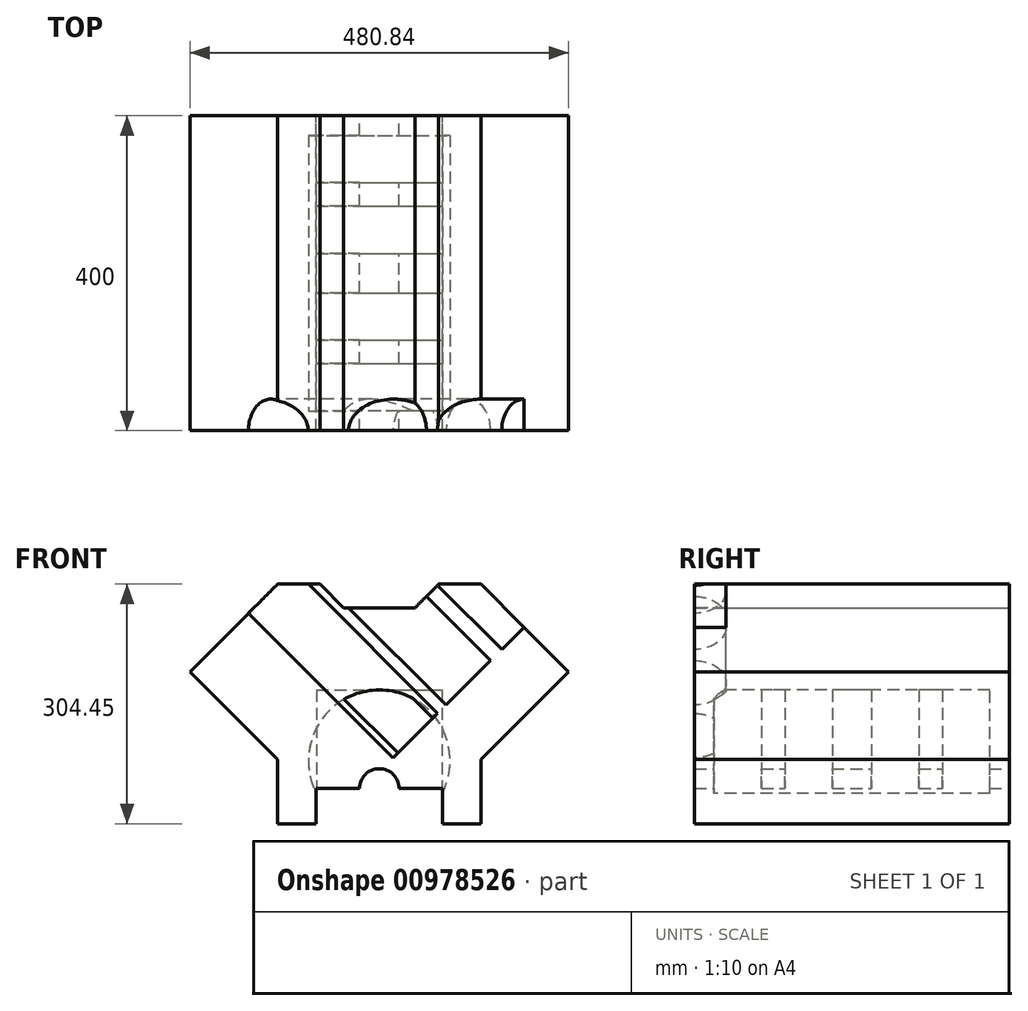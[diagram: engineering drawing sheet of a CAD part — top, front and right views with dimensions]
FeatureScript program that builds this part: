
annotation { "Feature Type Name" : "Feature", "Feature Type Description" : "" }
export const myFeature = defineFeature(function(context is Context, id is Id, definition is map)
    precondition{}
    {
        {
            var Q0;
            Q0=qCreatedBy(makeId("Front.planeOp"),FACE);
            var sketch = newSketch(context, id + "F0", { "sketchPlane" : qUnion([Q0])});
            skCircle(sketch, "E0", {"center": v(0, 0) * mm, "radius": 25 * mm});
            skLineSegment(sketch, "E1", {"start": v(0, 0) * mm, "end": v(-25, 0) * mm});
            skLineSegment(sketch, "E2", {"start": v(0, 0) * mm, "end": v(0, 157.92) * mm, "construction": true});
            skLineSegment(sketch, "E3", {"start": v(0, 0) * mm, "end": v(-17.68, 17.68) * mm, "construction": true});
            skLineSegment(sketch, "E4", {"start": v(0, 0) * mm, "end": v(28.28, 28.28) * mm, "construction": true});
            skLineSegment(sketch, "E5.0", {"start": v(-79.55, -80) * mm, "end": v(-129.1, -80) * mm});
            skLineSegment(sketch, "E6", {"start": v(-240.42, 113.14) * mm, "end": v(-148.5, 205.06) * mm, "construction": true});
            skLineSegment(sketch, "E7", {"start": v(0, 157.92) * mm, "end": v(0, 224.45) * mm, "construction": true});
            skLineSegment(sketch, "E8", {"start": v(-148.5, 205.06) * mm, "end": v(-129.1, 224.45) * mm, "construction": true});
            skLineSegment(sketch, "E9", {"start": v(-129.1, 224.45) * mm, "end": v(0, 224.45) * mm, "construction": true});
            skLineSegment(sketch, "E10", {"start": v(-129.1, 1.82) * mm, "end": v(-129.1, -40) * mm, "construction": true});
            skLineSegment(sketch, "E11", {"start": v(-129.1, -40) * mm, "end": v(-129.1, -80) * mm, "construction": true});
            skLineSegment(sketch, "E12.trimOffspring", {"start": v(-129.1, 1.82) * mm, "end": v(-240.42, 113.14) * mm});
            skLineSegment(sketch, "E13", {"start": v(0, 224.45) * mm, "end": v(-129.1, 224.45) * mm});
            skLineSegment(sketch, "E14", {"start": v(-240.42, 113.14) * mm, "end": v(-129.1, 224.45) * mm});
            skLineSegment(sketch, "E15", {"start": v(-129.1, 1.82) * mm, "end": v(-129.1, -80) * mm});
            skLineSegment(sketch, "E16.MirrorCS", {"start": v(129.1, 224.45) * mm, "end": v(0, 224.45) * mm, "construction": true});
            skLineSegment(sketch, "E17.MirrorCS", {"start": v(148.5, 205.06) * mm, "end": v(129.1, 224.45) * mm, "construction": true});
            skLineSegment(sketch, "E18.MirrorCS", {"start": v(240.42, 113.14) * mm, "end": v(148.5, 205.06) * mm, "construction": true});
            skLineSegment(sketch, "E19.MirrorCS", {"start": v(129.1, 1.82) * mm, "end": v(240.42, 113.14) * mm});
            skLineSegment(sketch, "E20.MirrorCS", {"start": v(129.1, 1.82) * mm, "end": v(129.1, -40) * mm, "construction": true});
            skLineSegment(sketch, "E21.MirrorCS", {"start": v(129.1, -40) * mm, "end": v(129.1, -80) * mm, "construction": true});
            skLineSegment(sketch, "E22.MirrorCS", {"start": v(79.55, -80) * mm, "end": v(129.1, -80) * mm});
            skPoint(sketch, "E23.cornerSnap0", {"position": v(79.55, -80) * mm});
            skPoint(sketch, "E24.MirrorCS.end.orphan", {"position": v(30, -80) * mm});
            skLineSegment(sketch, "E25", {"start": v(-79.55, -80) * mm, "end": v(-79.55, -39.1) * mm});
            skPoint(sketch, "E25.endSnap0", {"position": v(-129.1, -39.1) * mm});
            skLineSegment(sketch, "E26", {"start": v(79.55, -40) * mm, "end": v(79.55, -80) * mm});
            skArc(sketch, "E27", {"start": v(79.55, -42.1) * mm, "mid": v(0, 90) * mm, "end": v(-79.55, -42.1) * mm});
            skLineSegment(sketch, "E28", {"start": v(0, 0) * mm, "end": v(256.96, 256.96) * mm, "construction": true});
            skLineSegment(sketch, "E29", {"start": v(0, 0) * mm, "end": v(-256.18, 256.18) * mm, "construction": true});
            skLineSegment(sketch, "E30", {"start": v(0, 224.45) * mm, "end": v(129.1, 224.45) * mm});
            skLineSegment(sketch, "E31", {"start": v(240.42, 113.14) * mm, "end": v(129.1, 224.45) * mm});
            skLineSegment(sketch, "E32", {"start": v(129.1, 1.82) * mm, "end": v(129.1, -80) * mm});
            skSolve(sketch);
        }
        {
            var Q0;
            {var subQ4=sQuery(id+"F0.wireOp",EDGE,"E5.0");Q0=makeQuery(id+"F0.imprint","IMPRINT",FACE,{"disambiguationData":[TD([[makeQuery(id+"F0.imprint","IMPRINT",EDGE,{"derivedFrom":subQ4}),-1.0]])]});}
            extrude(context, id + "F1", {"entities" : qUnion([Q0]), "oppositeDirection" : true, "depth" : 400 * mm, "offsetDistance" : 25 * mm});
        }
        {
            var Q0;
            Q0=makeQuery(id+"F1.opExtrude","CAP_FACE",FACE,{"disambiguationData":[OSD([sQuery(id+"F0.wireOp",EDGE,"E5.0"),sQuery(id+"F0.wireOp",EDGE,"E12.trimOffspring"),sQuery(id+"F0.wireOp",EDGE,"E13"),sQuery(id+"F0.wireOp",EDGE,"E14"),sQuery(id+"F0.wireOp",EDGE,"E15"),sQuery(id+"F0.wireOp",EDGE,"E19.MirrorCS"),sQuery(id+"F0.wireOp",EDGE,"E22.MirrorCS"),sQuery(id+"F0.wireOp",EDGE,"E25"),sQuery(id+"F0.wireOp",EDGE,"E26"),sQuery(id+"F0.wireOp",EDGE,"E27"),sQuery(id+"F0.wireOp",EDGE,"E30"),sQuery(id+"F0.wireOp",EDGE,"E31"),sQuery(id+"F0.wireOp",EDGE,"E32")])],"isStart":true});
            var sketch = newSketch(context, id + "F2", { "sketchPlane" : qUnion([Q0])});
            skLineSegment(sketch, "E33.bottom", {"start": v(-100.58, 95.3) * mm, "end": v(104.32, 95.3) * mm});
            skLineSegment(sketch, "E33.top", {"start": v(-100.58, -80) * mm, "end": v(104.32, -80) * mm});
            skLineSegment(sketch, "E33.left", {"start": v(-100.58, 95.3) * mm, "end": v(-100.58, -80) * mm});
            skLineSegment(sketch, "E33.right", {"start": v(104.32, 95.3) * mm, "end": v(104.32, -80) * mm});
            skSolve(sketch);
        }
        {
            var Q0;
            Q0 = qSketchRegion(id + "F2", true);
            extrude(context, id + "F3", {"entities" : qUnion([Q0]), "operationType" : NewBodyOperationType.ADD, "oppositeDirection" : true, "depth" : 25 * mm, "offsetDistance" : 25 * mm});
        }
        {
            var Q0;
            Q0=makeQuery(id+"F1.opExtrude","CAP_FACE",FACE,{"disambiguationData":[OSD([sQuery(id+"F0.wireOp",EDGE,"E5.0"),sQuery(id+"F0.wireOp",EDGE,"E12.trimOffspring"),sQuery(id+"F0.wireOp",EDGE,"E13"),sQuery(id+"F0.wireOp",EDGE,"E14"),sQuery(id+"F0.wireOp",EDGE,"E15"),sQuery(id+"F0.wireOp",EDGE,"E19.MirrorCS"),sQuery(id+"F0.wireOp",EDGE,"E22.MirrorCS"),sQuery(id+"F0.wireOp",EDGE,"E25"),sQuery(id+"F0.wireOp",EDGE,"E26"),sQuery(id+"F0.wireOp",EDGE,"E27"),sQuery(id+"F0.wireOp",EDGE,"E30"),sQuery(id+"F0.wireOp",EDGE,"E31"),sQuery(id+"F0.wireOp",EDGE,"E32")])],"isStart":false});
            var sketch = newSketch(context, id + "F4", { "sketchPlane" : qUnion([Q0])});
            skLineSegment(sketch, "E34.bottom", {"start": v(-94.74, 103.1) * mm, "end": v(97.32, 103.1) * mm});
            skLineSegment(sketch, "E34.top", {"start": v(-94.74, -80) * mm, "end": v(97.32, -80) * mm});
            skLineSegment(sketch, "E34.left", {"start": v(-94.74, 103.1) * mm, "end": v(-94.74, -80) * mm});
            skLineSegment(sketch, "E34.right", {"start": v(97.32, 103.1) * mm, "end": v(97.32, -80) * mm});
            skSolve(sketch);
        }
        {
            var Q0;
            Q0 = qSketchRegion(id + "F4", true);
            extrude(context, id + "F5", {"entities" : qUnion([Q0]), "operationType" : NewBodyOperationType.ADD, "oppositeDirection" : true, "depth" : 25 * mm, "offsetDistance" : 25 * mm});
        }
        {
            var Q0;
            Q0=makeQuery(id+"F5.boolean.opBoolean","MERGE",FACE,{"derivedFrom":[makeQuery(id+"F3.boolean.opBoolean","MERGE",FACE,{"derivedFrom":[makeQuery(id+"F1.opExtrude","SWEPT_FACE",FACE,{"disambiguationData":[OSD([sQuery(id+"F0.wireOp",EDGE,"E5.0")])]}),makeQuery(id+"F1.opExtrude","SWEPT_FACE",FACE,{"disambiguationData":[OSD([sQuery(id+"F0.wireOp",EDGE,"E22.MirrorCS")])]}),makeQuery(id+"F3.opExtrude","SWEPT_FACE",FACE,{"disambiguationData":[OSD([sQuery(id+"F2.wireOp",EDGE,"E33.top")])]})]}),makeQuery(id+"F5.opExtrude","SWEPT_FACE",FACE,{"disambiguationData":[OSD([sQuery(id+"F4.wireOp",EDGE,"E34.top")])]})]});
            var sketch = newSketch(context, id + "F6", { "sketchPlane" : qUnion([Q0])});
            skLineSegment(sketch, "E35", {"start": v(0, 0) * mm, "end": v(0, -575.14) * mm});
            skLineSegment(sketch, "E36.left", {"start": v(-79.55, -216.72) * mm, "end": v(-79.55, -181.56) * mm});
            skLineSegment(sketch, "E37.left", {"start": v(-79.55, -112.96) * mm, "end": v(-79.55, -81.24) * mm});
            skLineSegment(sketch, "E37.right", {"start": v(79.55, -92.5) * mm, "end": v(79.55, -81.24) * mm});
            skLineSegment(sketch, "E38.left", {"start": v(-79.55, -318.76) * mm, "end": v(-79.55, -285.32) * mm});
            skLineSegment(sketch, "E38.right", {"start": v(79.55, -318.76) * mm, "end": v(79.55, -285.32) * mm});
            skLineSegment(sketch, "E39.0", {"start": v(79.55, -375) * mm, "end": v(79.55, -227.5) * mm, "construction": true});
            skLineSegment(sketch, "E39.1", {"start": v(-79.55, -375) * mm, "end": v(-79.55, -318.76) * mm, "construction": true});
            skLineSegment(sketch, "E39.2", {"start": v(-79.55, -25) * mm, "end": v(79.55, -25) * mm, "construction": true});
            skLineSegment(sketch, "E39.3", {"start": v(79.55, -375) * mm, "end": v(-79.55, -375) * mm, "construction": true});
            skLineSegment(sketch, "E40.trimOffspring", {"start": v(-79.55, -285.32) * mm, "end": v(-79.55, -25) * mm, "construction": true});
            skLineSegment(sketch, "E41.trimOffspring", {"start": v(79.55, -172.5) * mm, "end": v(79.55, -92.5) * mm, "construction": true});
            skLineSegment(sketch, "E42.trimOffspring", {"start": v(79.55, -81.24) * mm, "end": v(79.55, -25) * mm, "construction": true});
            skLineSegment(sketch, "E43", {"start": v(-129.1, -200) * mm, "end": v(324.31, -200) * mm, "construction": true});
            skLineSegment(sketch, "E44.left", {"start": v(79.55, -172.5) * mm, "end": v(79.55, -147.5) * mm});
            skLineSegment(sketch, "E44.right", {"start": v(-79.55, -172.5) * mm, "end": v(-79.55, -147.5) * mm});
            skLineSegment(sketch, "E45.left", {"start": v(79.55, -227.5) * mm, "end": v(79.55, -252.5) * mm});
            skLineSegment(sketch, "E45.right", {"start": v(-79.55, -227.5) * mm, "end": v(-79.55, -252.5) * mm});
            skLineSegment(sketch, "E46.left", {"start": v(79.55, -92.5) * mm, "end": v(79.55, -67.5) * mm});
            skLineSegment(sketch, "E46.right", {"start": v(-79.55, -92.5) * mm, "end": v(-79.55, -67.5) * mm});
            skLineSegment(sketch, "E47.left", {"start": v(79.55, -307.5) * mm, "end": v(79.55, -332.5) * mm});
            skLineSegment(sketch, "E47.right", {"start": v(-79.55, -307.5) * mm, "end": v(-79.55, -332.5) * mm});
            skLineSegment(sketch, "E48.bottom", {"start": v(-79.55, -175) * mm, "end": v(79.55, -175) * mm});
            skLineSegment(sketch, "E48.top", {"start": v(-79.55, -225) * mm, "end": v(79.55, -225) * mm});
            skLineSegment(sketch, "E48.left", {"start": v(-79.55, -175) * mm, "end": v(-79.55, -225) * mm});
            skLineSegment(sketch, "E48.right", {"start": v(79.55, -175) * mm, "end": v(79.55, -225) * mm});
            skPoint(sketch, "E48.middle", {"position": v(0, -200) * mm});
            skLineSegment(sketch, "E49.bottom", {"start": v(-79.55, -285) * mm, "end": v(79.55, -285) * mm});
            skLineSegment(sketch, "E49.top", {"start": v(-79.55, -315) * mm, "end": v(79.55, -315) * mm});
            skLineSegment(sketch, "E49.left", {"start": v(-79.55, -285) * mm, "end": v(-79.55, -315) * mm});
            skLineSegment(sketch, "E49.right", {"start": v(79.55, -285) * mm, "end": v(79.55, -315) * mm});
            skPoint(sketch, "E49.middle", {"position": v(0, -300) * mm});
            skLineSegment(sketch, "E50.MirrorCS", {"start": v(-79.55, -85) * mm, "end": v(79.55, -85) * mm});
            skLineSegment(sketch, "E51.MirrorCS", {"start": v(-79.55, -115) * mm, "end": v(79.55, -115) * mm});
            skLineSegment(sketch, "E52.bottom", {"start": v(79.55, -115) * mm, "end": v(-79.55, -115) * mm});
            skLineSegment(sketch, "E52.top", {"start": v(79.55, -85) * mm, "end": v(-79.55, -85) * mm});
            skLineSegment(sketch, "E52.left", {"start": v(79.55, -115) * mm, "end": v(79.55, -85) * mm});
            skLineSegment(sketch, "E52.right", {"start": v(-79.55, -115) * mm, "end": v(-79.55, -85) * mm});
            skSolve(sketch);
        }
        {
            var Q0;
            {var subQ6=sQuery(id+"F6.wireOp",EDGE,"E48.right");var subQ10=sQuery(id+"F6.wireOp",EDGE,"E52.left");var subQ19=sQuery(id+"F6.wireOp",EDGE,"E36.left");var subQ24=sQuery(id+"F6.wireOp",EDGE,"E52.right");var subQ25=sQuery(id+"F6.wireOp",EDGE,"E49.right");var subQ34=sQuery(id+"F6.wireOp",EDGE,"E49.left");Q0=qUnion([makeQuery(id+"F6.imprint","IMPRINT",FACE,{"disambiguationData":[TD([[makeQuery(id+"F6.imprint","IMPRINT",EDGE,{"derivedFrom":subQ34}),-1.0]])]}),makeQuery(id+"F6.imprint","IMPRINT",FACE,{"disambiguationData":[TD([[makeQuery(id+"F6.imprint","IMPRINT",EDGE,{"derivedFrom":subQ25}),1.0]])]}),makeQuery(id+"F6.imprint","IMPRINT",FACE,{"disambiguationData":[TD([[makeQuery(id+"F6.imprint","IMPRINT",EDGE,{"derivedFrom":subQ24}),-1.0]])]}),makeQuery(id+"F6.imprint","IMPRINT",FACE,{"disambiguationData":[TD([[makeQuery(id+"F6.imprint","IMPRINT",EDGE,{"derivedFrom":subQ19}),-1.0]])]}),makeQuery(id+"F6.imprint","IMPRINT",FACE,{"disambiguationData":[TD([[makeQuery(id+"F6.imprint","IMPRINT",EDGE,{"derivedFrom":subQ10}),1.0]])]}),makeQuery(id+"F6.imprint","IMPRINT",FACE,{"disambiguationData":[TD([[makeQuery(id+"F6.imprint","IMPRINT",EDGE,{"derivedFrom":subQ6}),1.0]])]})]);}
            extrude(context, id + "F7", {"entities" : qUnion([Q0]), "oppositeDirection" : true, "depth" : 170 * mm, "offsetDistance" : 25 * mm});
        }
        {
            var Q0;
            Q0=makeQuery(id+"F5.boolean.opBoolean","MERGE",FACE,{"derivedFrom":[makeQuery(id+"F1.opExtrude","CAP_FACE",FACE,{"disambiguationData":[OSD([sQuery(id+"F0.wireOp",EDGE,"E5.0"),sQuery(id+"F0.wireOp",EDGE,"E12.trimOffspring"),sQuery(id+"F0.wireOp",EDGE,"E13"),sQuery(id+"F0.wireOp",EDGE,"E14"),sQuery(id+"F0.wireOp",EDGE,"E15"),sQuery(id+"F0.wireOp",EDGE,"E19.MirrorCS"),sQuery(id+"F0.wireOp",EDGE,"E22.MirrorCS"),sQuery(id+"F0.wireOp",EDGE,"E25"),sQuery(id+"F0.wireOp",EDGE,"E26"),sQuery(id+"F0.wireOp",EDGE,"E27"),sQuery(id+"F0.wireOp",EDGE,"E30"),sQuery(id+"F0.wireOp",EDGE,"E31"),sQuery(id+"F0.wireOp",EDGE,"E32")])],"isStart":false}),makeQuery(id+"F5.opExtrude","CAP_FACE",FACE,{"disambiguationData":[OSD([sQuery(id+"F4.wireOp",EDGE,"E34.bottom"),sQuery(id+"F4.wireOp",EDGE,"E34.top"),sQuery(id+"F4.wireOp",EDGE,"E34.left"),sQuery(id+"F4.wireOp",EDGE,"E34.right")])],"isStart":true})]});
            var sketch = newSketch(context, id + "F8", { "sketchPlane" : qUnion([Q0])});
            skLineSegment(sketch, "E53", {"start": v(0, -156.26) * mm, "end": v(0, -80) * mm, "construction": true});
            skPoint(sketch, "E53.endSnap0", {"position": v(0, 224.45) * mm});
            skLineSegment(sketch, "E54", {"start": v(0, 194.45) * mm, "end": v(-45.42, 194.45) * mm});
            skLineSegment(sketch, "E55", {"start": v(-45.42, 194.45) * mm, "end": v(-102.54, 251.57) * mm});
            skLineSegment(sketch, "E56.MirrorCS", {"start": v(0, 194.45) * mm, "end": v(45.42, 194.45) * mm});
            skLineSegment(sketch, "E57.MirrorCS", {"start": v(45.42, 194.45) * mm, "end": v(102.54, 251.57) * mm});
            skLineSegment(sketch, "E58.bottom", {"start": v(0, -80) * mm, "end": v(-80, -80) * mm});
            skLineSegment(sketch, "E58.top", {"start": v(-25, -35) * mm, "end": v(-80, -35) * mm});
            skLineSegment(sketch, "E58.left", {"start": v(0, -80) * mm, "end": v(0, -35) * mm});
            skLineSegment(sketch, "E58.right", {"start": v(-80, -80) * mm, "end": v(-80, -35) * mm});
            skArc(sketch, "E59", {"start": v(25, -35) * mm, "mid": v(0, -10) * mm, "end": v(-25, -35) * mm});
            skLineSegment(sketch, "E60.MirrorCS", {"start": v(25, -35) * mm, "end": v(80, -35) * mm});
            skLineSegment(sketch, "E61.MirrorCS", {"start": v(0, -80) * mm, "end": v(80, -80) * mm});
            skLineSegment(sketch, "E62.MirrorCS", {"start": v(80, -80) * mm, "end": v(80, -35) * mm});
            skLineSegment(sketch, "E63.trimOffspring", {"start": v(0, -35) * mm, "end": v(0, 269.26) * mm, "construction": true});
            skLineSegment(sketch, "E64", {"start": v(-102.54, 251.57) * mm, "end": v(102.54, 251.57) * mm});
            skSolve(sketch);
        }
        {
            var Q0;
            Q0 = qSketchRegion(id + "F8", true);
            extrude(context, id + "F9", {"entities" : qUnion([Q0]), "operationType" : NewBodyOperationType.REMOVE, "oppositeDirection" : true, "depth" : 400 * mm, "offsetDistance" : 25 * mm});
        }
        {
            var Q0;
            Q0=makeQuery(id+"F1.opExtrude","SWEPT_FACE",FACE,{"disambiguationData":[OSD([sQuery(id+"F0.wireOp",EDGE,"E14")])]});
            var sketch = newSketch(context, id + "F10", { "sketchPlane" : qUnion([Q0])});
            skLineSegment(sketch, "E65.0", {"start": v(-90, 400) * mm, "end": v(-90, 0) * mm});
            skLineSegment(sketch, "E65.1", {"start": v(-90, 400) * mm, "end": v(67.43, 400) * mm});
            skLineSegment(sketch, "E65.2", {"start": v(67.43, 400) * mm, "end": v(67.43, 0) * mm});
            skCircle(sketch, "E66", {"center": v(0, 345) * mm, "radius": 40 * mm});
            skCircle(sketch, "E67", {"center": v(0, 250) * mm, "radius": 40 * mm});
            skCircle(sketch, "E68", {"center": v(0, 150) * mm, "radius": 40 * mm});
            skCircle(sketch, "E69", {"center": v(0, 55) * mm, "radius": 40 * mm});
            skLineSegment(sketch, "E70", {"start": v(-148.8, 200) * mm, "end": v(117.34, 200) * mm, "construction": true});
            skPoint(sketch, "E70.startSnap0", {"position": v(-90, 200) * mm});
            skLineSegment(sketch, "E71", {"start": v(0, 395.1) * mm, "end": v(0, -33.4) * mm, "construction": true});
            skSolve(sketch);
        }
        {
            var Q0;
            Q0 = qSketchRegion(id + "F10", true);
            extrude(context, id + "F11", {"entities" : qUnion([Q0]), "operationType" : NewBodyOperationType.REMOVE, "oppositeDirection" : true, "depth" : 260 * mm, "offsetDistance" : 25 * mm});
        }
    });
